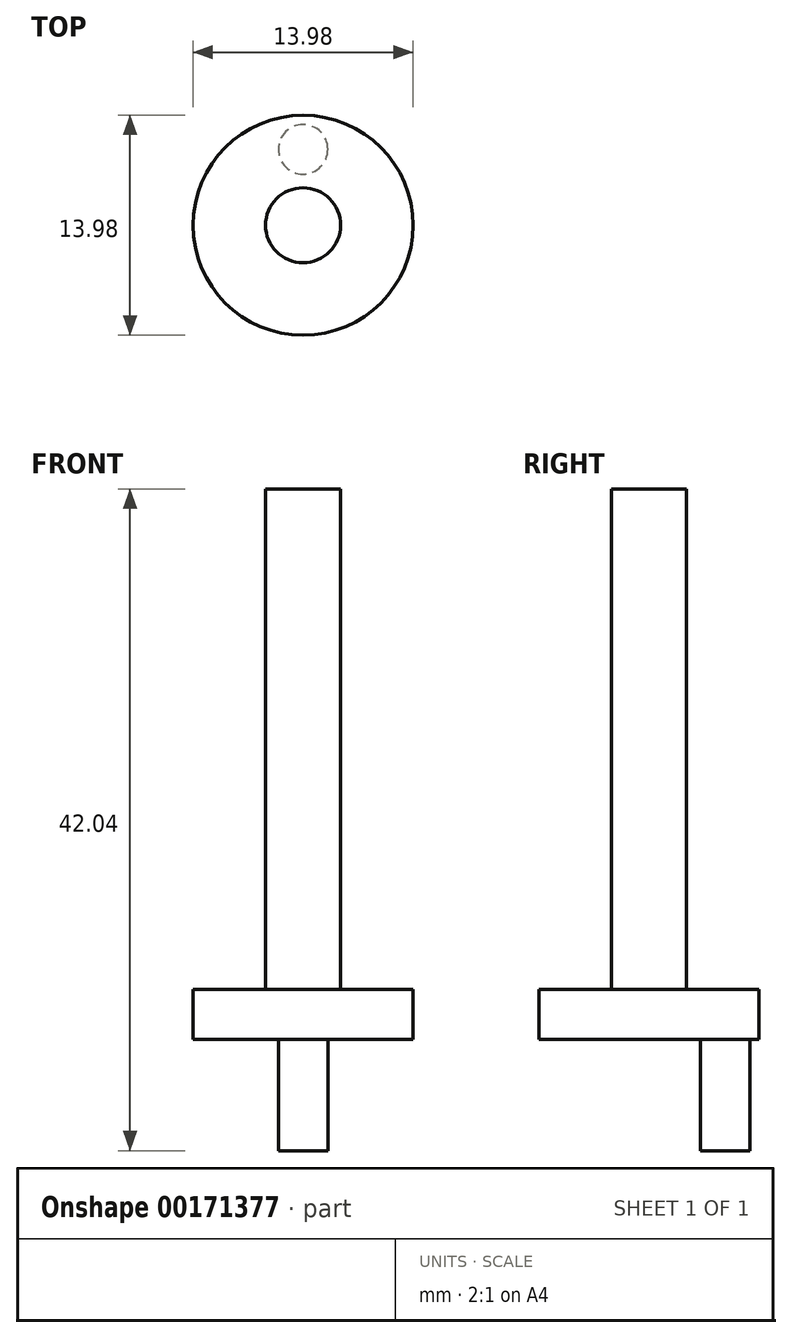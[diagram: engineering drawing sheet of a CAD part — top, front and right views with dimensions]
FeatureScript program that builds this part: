
annotation { "Feature Type Name" : "Feature", "Feature Type Description" : "" }
export const myFeature = defineFeature(function(context is Context, id is Id, definition is map)
    precondition{}
    {
        {
            var Q0;
            Q0=qCreatedBy(makeId("Top.planeOp"),FACE);
            var sketch = newSketch(context, id + "F0", { "sketchPlane" : qUnion([Q0])});
            skCircle(sketch, "E0", {"center": v(0, 0) * mm, "radius": 6.99 * mm});
            skCircle(sketch, "E1", {"center": v(0, 4.83) * mm, "radius": 1.57 * mm});
            skCircle(sketch, "E2", {"center": v(0, 0) * mm, "radius": 2.38 * mm});
            skSolve(sketch);
        }
        {
            var Q0;
            Q0=makeQuery(id+"F0.imprint","IMPRINT",FACE,{"disambiguationData":[TD([[makeQuery(id+"F0.imprint","IMPRINT",EDGE,{"derivedFrom":sQuery(id+"F0.wireOp",EDGE,"E0")}),1.0]])]});
            var Q1;
            Q1=makeQuery(id+"F0.imprint","IMPRINT",FACE,{"disambiguationData":[TD([[makeQuery(id+"F0.imprint","IMPRINT",EDGE,{"derivedFrom":sQuery(id+"F0.wireOp",EDGE,"E1")}),1.0]])]});
            extrude(context, id + "F1", {"entities" : qUnion([Q0, Q1]), "depth" : 3.17 * mm});
        }
        {
            var Q0;
            Q0=makeQuery(id+"F0.imprint","IMPRINT",FACE,{"disambiguationData":[TD([[makeQuery(id+"F0.imprint","IMPRINT",EDGE,{"derivedFrom":sQuery(id+"F0.wireOp",EDGE,"E2")}),1.0]])]});
            extrude(context, id + "F2", {"entities" : qUnion([Q0]), "operationType" : NewBodyOperationType.ADD, "depth" : 34.98 * mm});
        }
        {
            var Q0;
            Q0=makeQuery(id+"F0.imprint","IMPRINT",FACE,{"disambiguationData":[TD([[makeQuery(id+"F0.imprint","IMPRINT",EDGE,{"derivedFrom":sQuery(id+"F0.wireOp",EDGE,"E1")}),1.0]])]});
            var Q1;
            Q1=sQuery(id+"F0.wireOp",EDGE,"E1");
            extrude(context, id + "F3", {"entities" : qUnion([Q0]), "operationType" : NewBodyOperationType.ADD, "surfaceEntities" : qUnion([Q1]), "oppositeDirection" : true, "depth" : 7.06 * mm});
        }
    });
